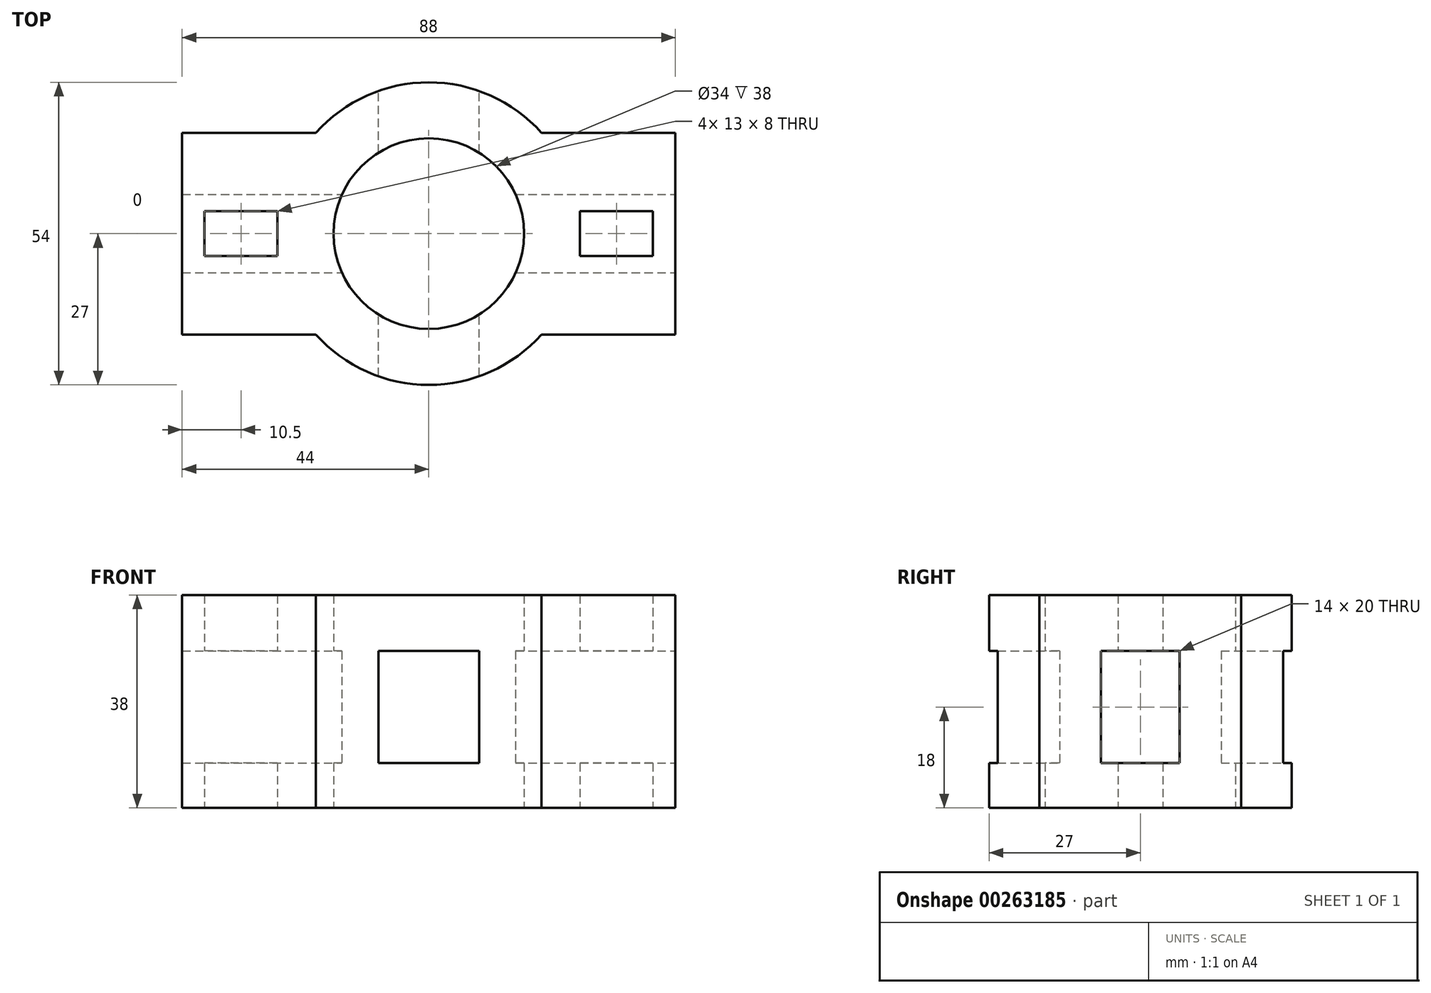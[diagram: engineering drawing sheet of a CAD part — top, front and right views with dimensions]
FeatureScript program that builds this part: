
annotation { "Feature Type Name" : "Feature", "Feature Type Description" : "" }
export const myFeature = defineFeature(function(context is Context, id is Id, definition is map)
    precondition{}
    {
        {
            var Q0;
            Q0=qCreatedBy(makeId("Top.planeOp"),FACE);
            var sketch = newSketch(context, id + "F0", { "sketchPlane" : qUnion([Q0])});
            skLineSegment(sketch, "E0.bottom", {"start": v(44, -18) * mm, "end": v(20.12, -18) * mm});
            skLineSegment(sketch, "E0.top", {"start": v(44, 18) * mm, "end": v(20.12, 18) * mm});
            skLineSegment(sketch, "E0.left", {"start": v(44, -18) * mm, "end": v(44, 18) * mm});
            skLineSegment(sketch, "E0.right", {"start": v(-44, -18) * mm, "end": v(-44, 18) * mm});
            skPoint(sketch, "E0.middle", {"position": v(0, 0) * mm});
            skArc(sketch, "E1", {"start": v(20.12, 18) * mm, "mid": v(0, 27) * mm, "end": v(-20.12, 18) * mm});
            skPoint(sketch, "E2", {"position": v(20.12, -18) * mm});
            skPoint(sketch, "E3", {"position": v(-20.12, -18) * mm});
            skPoint(sketch, "E4", {"position": v(-20.12, 18) * mm});
            skPoint(sketch, "E5", {"position": v(20.12, 18) * mm});
            skLineSegment(sketch, "E6.trimOffspring", {"start": v(-20.12, 18) * mm, "end": v(-44, 18) * mm});
            skLineSegment(sketch, "E7.trimOffspring", {"start": v(-20.12, -18) * mm, "end": v(-44, -18) * mm});
            skCircle(sketch, "E8", {"center": v(0, 0) * mm, "radius": 17 * mm});
            skLineSegment(sketch, "E9.bottom", {"start": v(-27, -4) * mm, "end": v(-40, -4) * mm});
            skLineSegment(sketch, "E9.top", {"start": v(-27, 4) * mm, "end": v(-40, 4) * mm});
            skLineSegment(sketch, "E9.left", {"start": v(-27, -4) * mm, "end": v(-27, 4) * mm});
            skLineSegment(sketch, "E9.right", {"start": v(-40, -4) * mm, "end": v(-40, 4) * mm});
            skPoint(sketch, "E9.middle", {"position": v(-33.5, 0) * mm});
            skLineSegment(sketch, "E10.bottom", {"start": v(40, -4) * mm, "end": v(27, -4) * mm});
            skLineSegment(sketch, "E10.top", {"start": v(40, 4) * mm, "end": v(27, 4) * mm});
            skLineSegment(sketch, "E10.left", {"start": v(40, -4) * mm, "end": v(40, 4) * mm});
            skLineSegment(sketch, "E10.right", {"start": v(27, -4) * mm, "end": v(27, 4) * mm});
            skPoint(sketch, "E10.middle", {"position": v(33.5, 0) * mm});
            skArc(sketch, "E11.trimOffspring", {"start": v(-20.12, -18) * mm, "mid": v(0, -27) * mm, "end": v(20.12, -18) * mm});
            skSolve(sketch);
        }
        {
            var Q0;
            Q0 = qSketchRegion(id + "F0", true);
            extrude(context, id + "F4", {"entities" : qUnion([Q0]), "depth" : 38 * mm});
        }
        {
            var Q0;
            Q0=qCreatedBy(makeId("Front.planeOp"),FACE);
            var sketch = newSketch(context, id + "F1", { "sketchPlane" : qUnion([Q0])});
            skLineSegment(sketch, "E12.bottom", {"start": v(9, 28) * mm, "end": v(-9, 28) * mm});
            skLineSegment(sketch, "E12.top", {"start": v(9, 8) * mm, "end": v(-9, 8) * mm});
            skLineSegment(sketch, "E12.left", {"start": v(9, 28) * mm, "end": v(9, 8) * mm});
            skLineSegment(sketch, "E12.right", {"start": v(-9, 28) * mm, "end": v(-9, 8) * mm});
            skPoint(sketch, "E12.middle", {"position": v(0, 18) * mm});
            skSolve(sketch);
        }
        {
            var Q0;
            Q0 = qSketchRegion(id + "F1", true);
            extrude(context, id + "F2", {"entities" : qUnion([Q0]), "operationType" : NewBodyOperationType.REMOVE, "endBound" : BoundingType.THROUGH_ALL, "depth" : 25 * mm, "hasSecondDirection" : true, "secondDirectionOppositeDirection" : true, "secondDirectionDepth" : 62.1 * mm});
        }
        {
            var Q0;
            Q0=qCreatedBy(makeId("Right.planeOp"),FACE);
            var sketch = newSketch(context, id + "F5", { "sketchPlane" : qUnion([Q0])});
            skLineSegment(sketch, "E13.bottom", {"start": v(7, 8) * mm, "end": v(-7, 8) * mm});
            skLineSegment(sketch, "E13.top", {"start": v(7, 28) * mm, "end": v(-7, 28) * mm});
            skLineSegment(sketch, "E13.left", {"start": v(7, 8) * mm, "end": v(7, 28) * mm});
            skLineSegment(sketch, "E13.right", {"start": v(-7, 8) * mm, "end": v(-7, 28) * mm});
            skPoint(sketch, "E13.middle", {"position": v(0, 18) * mm});
            skSolve(sketch);
        }
        {
            var Q0;
            Q0 = qSketchRegion(id + "F5", true);
            extrude(context, id + "F3", {"entities" : qUnion([Q0]), "operationType" : NewBodyOperationType.REMOVE, "endBound" : BoundingType.THROUGH_ALL, "oppositeDirection" : true, "depth" : 25 * mm, "hasSecondDirection" : true, "secondDirectionOppositeDirection" : false, "secondDirectionDepth" : 80.9 * mm});
        }
    });
